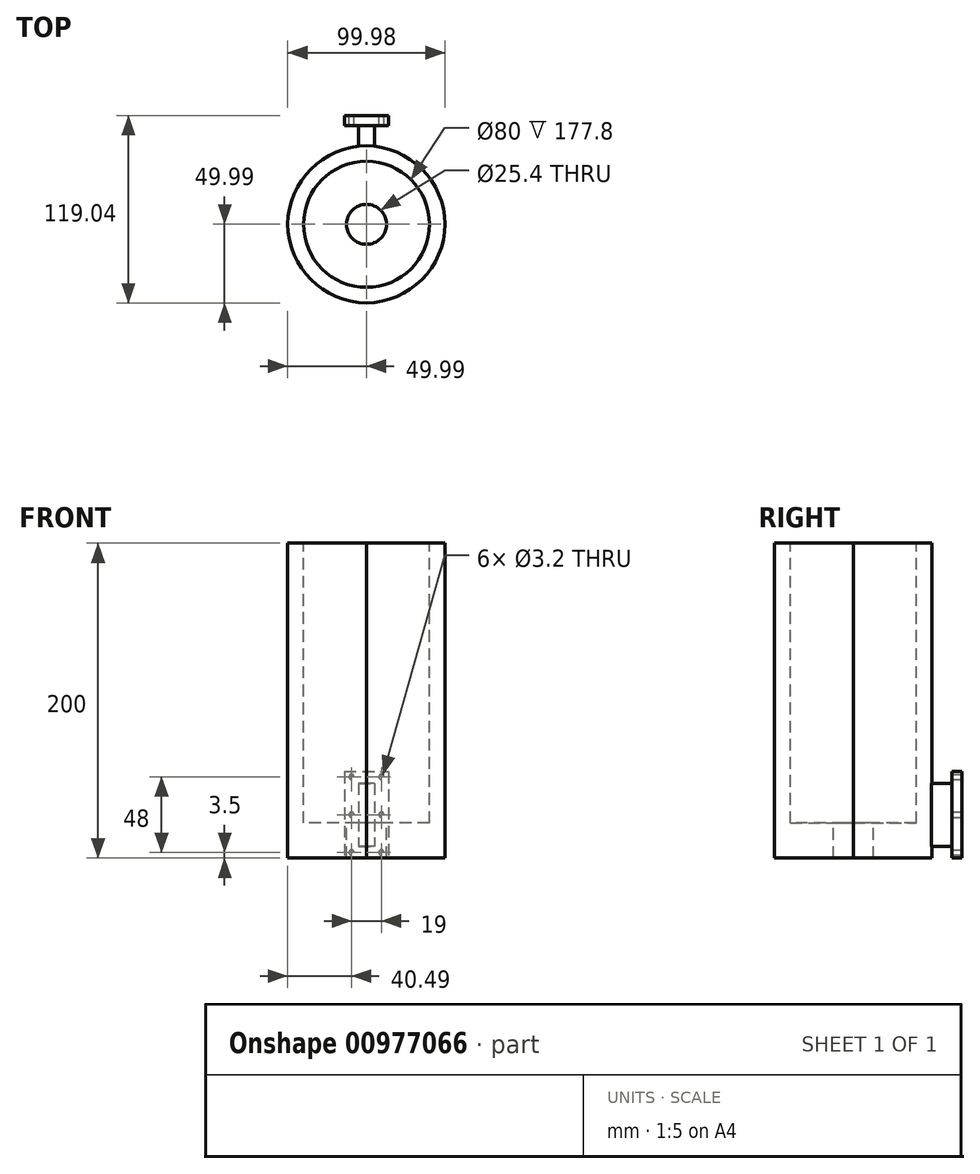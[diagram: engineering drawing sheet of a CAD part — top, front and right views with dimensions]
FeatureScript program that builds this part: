
annotation { "Feature Type Name" : "Feature", "Feature Type Description" : "" }
export const myFeature = defineFeature(function(context is Context, id is Id, definition is map)
    precondition{}
    {
        {
            var Q0;
            Q0=qCreatedBy(makeId("Front.planeOp"),FACE);
            var sketch = newSketch(context, id + "F0", { "sketchPlane" : qUnion([Q0])});
            skLineSegment(sketch, "E0.bottom", {"start": v(-14, 27.5) * mm, "end": v(14, 27.5) * mm});
            skLineSegment(sketch, "E0.top", {"start": v(-14, -27.5) * mm, "end": v(14, -27.5) * mm});
            skLineSegment(sketch, "E0.left", {"start": v(-14, 27.5) * mm, "end": v(-14, -27.5) * mm});
            skLineSegment(sketch, "E0.right", {"start": v(14, 27.5) * mm, "end": v(14, -27.5) * mm});
            skPoint(sketch, "E0.middle", {"position": v(0, 0) * mm});
            skCircle(sketch, "E1", {"center": v(-9.5, 0) * mm, "radius": 1.6 * mm});
            skLineSegment(sketch, "E2", {"start": v(0, 48.38) * mm, "end": v(0, -31.9) * mm, "construction": true});
            skPoint(sketch, "E2.endSnap0", {"position": v(0, -27.5) * mm});
            skCircle(sketch, "E3.MirrorC", {"center": v(9.5, 0) * mm, "radius": 1.6 * mm});
            skCircle(sketch, "E4.0.1.0", {"center": v(-9.5, 24) * mm, "radius": 1.6 * mm});
            skCircle(sketch, "E4.0.1.1", {"center": v(9.5, 24) * mm, "radius": 1.6 * mm});
            skLineSegment(sketch, "E4.direction1", {"start": v(-9.5, 0) * mm, "end": v(15.9, 0) * mm, "construction": true});
            skLineSegment(sketch, "E4.direction2", {"start": v(-9.5, 0) * mm, "end": v(-9.5, 24) * mm, "construction": true});
            skCircle(sketch, "E5.MirrorC", {"center": v(-9.5, -24) * mm, "radius": 1.6 * mm});
            skCircle(sketch, "E6.MirrorC", {"center": v(9.5, -24) * mm, "radius": 1.6 * mm});
            skSolve(sketch);
        }
        {
            var Q0;
            Q0=makeQuery(id+"F0.imprint","IMPRINT",FACE,{"disambiguationData":[TD([[makeQuery(id+"F0.imprint","IMPRINT",EDGE,{"derivedFrom":sQuery(id+"F0.wireOp",EDGE,"E0.bottom")}),-1.0]])]});
            extrude(context, id + "F1", {"entities" : qUnion([Q0]), "depth" : 6.35 * mm, "offsetDistance" : 25.4 * mm});
        }
        {
            var Q0;
            Q0=makeQuery(id+"F1.opExtrude","CAP_FACE",FACE,{"disambiguationData":[OSD([sQuery(id+"F0.wireOp",EDGE,"E0.bottom"),sQuery(id+"F0.wireOp",EDGE,"E0.top"),sQuery(id+"F0.wireOp",EDGE,"E0.left"),sQuery(id+"F0.wireOp",EDGE,"E0.right"),sQuery(id+"F0.wireOp",EDGE,"E1"),sQuery(id+"F0.wireOp",EDGE,"E3.MirrorC"),sQuery(id+"F0.wireOp",EDGE,"E4.0.1.0"),sQuery(id+"F0.wireOp",EDGE,"E4.0.1.1"),sQuery(id+"F0.wireOp",EDGE,"E5.MirrorC"),sQuery(id+"F0.wireOp",EDGE,"E6.MirrorC")])],"isStart":false});
            var sketch = newSketch(context, id + "F2", { "sketchPlane" : qUnion([Q0])});
            skLineSegment(sketch, "E7.bottom", {"start": v(-5, 20) * mm, "end": v(5, 20) * mm});
            skLineSegment(sketch, "E7.top", {"start": v(-5, -20) * mm, "end": v(5, -20) * mm});
            skLineSegment(sketch, "E7.left", {"start": v(-5, 20) * mm, "end": v(-5, -20) * mm});
            skLineSegment(sketch, "E7.right", {"start": v(5, 20) * mm, "end": v(5, -20) * mm});
            skPoint(sketch, "E7.middle", {"position": v(0, 0) * mm});
            skSolve(sketch);
        }
        {
            var Q0;
            Q0=qSketchRegion(id+"F2",true);
            extrude(context, id + "F3", {"entities" : qUnion([Q0]), "operationType" : NewBodyOperationType.ADD, "depth" : 12.7 * mm, "offsetDistance" : 25.4 * mm});
        }
        {
            var Q0;
            Q0=makeQuery(id+"F3.opExtrude","CAP_FACE",FACE,{"disambiguationData":[OSD([sQuery(id+"F2.wireOp",EDGE,"E7.bottom"),sQuery(id+"F2.wireOp",EDGE,"E7.top"),sQuery(id+"F2.wireOp",EDGE,"E7.left"),sQuery(id+"F2.wireOp",EDGE,"E7.right")])],"isStart":false});
            var sketch = newSketch(context, id + "F4", { "sketchPlane" : qUnion([Q0])});
            skPoint(sketch, "E8.middle", {"position": v(0, 0) * mm});
            skLineSegment(sketch, "E9.bottom", {"start": v(50, -27.5) * mm, "end": v(-50, -27.5) * mm});
            skLineSegment(sketch, "E9.top", {"start": v(50, 172.5) * mm, "end": v(-50, 172.5) * mm});
            skLineSegment(sketch, "E9.left", {"start": v(50, -27.5) * mm, "end": v(50, 172.5) * mm});
            skLineSegment(sketch, "E9.right", {"start": v(-50, -27.5) * mm, "end": v(-50, 172.5) * mm});
            skSolve(sketch);
        }
        {
            var Q0;
            Q0=qSketchRegion(id+"F4",true);
            extrude(context, id + "F5", {"entities" : qUnion([Q0]), "operationType" : NewBodyOperationType.ADD, "depth" : 100 * mm, "offsetDistance" : 25.4 * mm});
        }
        {
            var Q0;
            Q0=makeQuery(id+"F5.opExtrude","SWEPT_FACE",FACE,{"disambiguationData":[OSD([sQuery(id+"F4.wireOp",EDGE,"E9.top")])]});
            var sketch = newSketch(context, id + "F6", { "sketchPlane" : qUnion([Q0])});
            skLineSegment(sketch, "E10", {"start": v(0, -138.66) * mm, "end": v(0, 42.35) * mm, "construction": true});
            skPoint(sketch, "E10.startSnap0", {"position": v(0, -119.05) * mm});
            skCircle(sketch, "E11", {"center": v(0, -69.05) * mm, "radius": 40 * mm});
            skSolve(sketch);
        }
        {
            var Q0;
            Q0=qSketchRegion(id+"F6",true);
            extrude(context, id + "F7", {"entities" : qUnion([Q0]), "operationType" : NewBodyOperationType.REMOVE, "oppositeDirection" : true, "depth" : 177.8 * mm, "offsetDistance" : 25.4 * mm});
        }
        {
            var Q0;
            Q0=makeQuery(id+"F7.boolean.opBoolean","COPY",FACE,{"derivedFrom":makeQuery(id+"F7.opExtrude","CAP_FACE",FACE,{"disambiguationData":[OSD([sQuery(id+"F6.wireOp",EDGE,"E11")])],"isStart":false})});
            var sketch = newSketch(context, id + "F8", { "sketchPlane" : qUnion([Q0])});
            skCircle(sketch, "E12", {"center": v(0, -69.05) * mm, "radius": 12.7 * mm});
            skSolve(sketch);
        }
        {
            var Q0;
            Q0=qSketchRegion(id+"F8",true);
            extrude(context, id + "F9", {"entities" : qUnion([Q0]), "operationType" : NewBodyOperationType.REMOVE, "oppositeDirection" : true, "depth" : 41.66 * mm, "offsetDistance" : 25.4 * mm});
        }
        {
            var Q0;
            Q0=makeQuery(id+"F5.opExtrude","CAP_EDGE",EDGE,{"disambiguationData":[OSD([sQuery(id+"F4.wireOp",EDGE,"E9.left")])],"isStart":true});
            var Q1;
            Q1=makeQuery(id+"F5.opExtrude","CAP_EDGE",EDGE,{"disambiguationData":[OSD([sQuery(id+"F4.wireOp",EDGE,"E9.left")])],"isStart":false});
            var Q2;
            Q2=makeQuery(id+"F5.opExtrude","CAP_EDGE",EDGE,{"disambiguationData":[OSD([sQuery(id+"F4.wireOp",EDGE,"E9.right")])],"isStart":false});
            var Q3;
            Q3=makeQuery(id+"F5.opExtrude","CAP_EDGE",EDGE,{"disambiguationData":[OSD([sQuery(id+"F4.wireOp",EDGE,"E9.right")])],"isStart":true});
            fillet(context, id + "F10", {"entities" : qUnion([Q0, Q1, Q2, Q3]), "radius" : 50.8 * mm, "tangentPropagation" : true, "allowEdgeOverflow" : false});
        }
    });
